FCSTD DOCUMENT  (FreeCAD 0.16R6712 (Git))
Label: EuW
License: All rights reserved
LicenseURL: http://en.wikipedia.org/wiki/All_rights_reserved
objects: Sketcher::SketchObject×21, PartDesign::Pad×11, PartDesign::Pocket×10, App::DocumentObjectGroup×5, Mesh::Feature×4, Spreadsheet::Sheet×3, Image::ImagePlane×1, Part::Mirroring×1
note: 64 computed .brp shape members not serialized (recipe doc carries the construction recipe); baked Part::Feature solids carry a one-line shape summary decoded from their .brp

FEATURE [Sketcher::SketchObject] Sketch
  sketch-geometry (6):
    g0: LineSegment StartX=-20.6532 StartY=-31.9378 StartZ=0 EndX=22.2568 EndY=-31.9378 EndZ=0
    g1: LineSegment StartX=22.2568 StartY=-31.9378 StartZ=0 EndX=22.2568 EndY=-20.3155 EndZ=0
    g2: LineSegment StartX=22.2568 StartY=-20.3155 StartZ=0 EndX=19.6468 EndY=-11.9755 EndZ=0
    g3: LineSegment StartX=19.6468 StartY=-11.9755 StartZ=0 EndX=19.6468 EndY=32.5722 EndZ=0
    g4: LineSegment StartX=19.6468 StartY=32.5722 StartZ=0 EndX=-20.6532 EndY=32.5722 EndZ=0
    g5: LineSegment StartX=-20.6532 StartY=32.5722 StartZ=0 EndX=-20.6532 EndY=-31.9378 EndZ=0
  constraints (14):
    c: Horizontal(g0)
    c: Coincident(g0,g1)
    c: Vertical(g1)
    c: Coincident(g1,g2)
    c: Coincident(g2,g3)
    c: Vertical(g3)
    c: Coincident(g3,g4)
    c: Horizontal(g4)
    c: Coincident(g4,g5)
    c: Coincident(g5,g0)
    c: Vertical(g5)
    c: DistanceX(g0,g0) = 42.91
    c: DistanceY(g0,g4) = 64.51
    c: DistanceX(g2,g1) = 2.61
FEATURE [Image::ImagePlane] ImagePlane
  XSize = 52.4742
  YSize = 69.419
FEATURE [PartDesign::Pad] Pad
  Length = 25
  Length2 = 100
  Sketch = -> Sketch
  Type = 0
FEATURE [Sketcher::SketchObject] Sketch001
  ExternalGeometry = -> [Pad]
  Placement = pos=(0,0,25) rot=(0,0,1;0rad)
  Support = -> Pad [Face8]
  sketch-geometry (2):
    g0: Circle CenterX=-12.8432 CenterY=15.3222 CenterZ=0 NormalX=0 NormalY=0 NormalZ=1 Radius=5.15
    g1: Circle CenterX=9.30682 CenterY=15.3222 CenterZ=0 NormalX=0 NormalY=0 NormalZ=1 Radius=5.15
  constraints (6):
    c: Radius(g0) = 5.15
    c: DistanceX(g-3,g0) = 7.81
    c: Equal(g0,g1) = 5.15
    c: DistanceY(g0,g-3) = 17.25
    c: DistanceY(g1,g-3) = 17.25
    c: DistanceX(g0,g1) = 22.15
FEATURE [PartDesign::Pocket] Pocket
  Length = 5
  Sketch = -> Sketch001
  Type = 1
FEATURE [Sketcher::SketchObject] Sketch002
  expr: Constraints[13] = Spreadsheet.E2
  expr: Constraints[12] = Spreadsheet.C2
  expr: Constraints[11] = Spreadsheet.B2
  sketch-geometry (6):
    g0: LineSegment StartX=-20.6044 StartY=-32.0766 StartZ=0 EndX=22.3056 EndY=-32.0766 EndZ=0
    g1: LineSegment StartX=22.3056 StartY=-32.0766 StartZ=0 EndX=22.3056 EndY=-20.3155 EndZ=0
    g2: LineSegment StartX=22.3056 StartY=-20.3155 StartZ=0 EndX=19.6956 EndY=-11.9755 EndZ=0
    g3: LineSegment StartX=19.6956 StartY=-11.9755 StartZ=0 EndX=19.6956 EndY=32.4334 EndZ=0
    g4: LineSegment StartX=19.6956 StartY=32.4334 StartZ=0 EndX=-20.6044 EndY=32.4334 EndZ=0
    g5: LineSegment StartX=-20.6044 StartY=32.4334 StartZ=0 EndX=-20.6044 EndY=-32.0766 EndZ=0
  constraints (14):
    c: Horizontal(g0)
    c: Coincident(g0,g1)
    c: Vertical(g1)
    c: Coincident(g1,g2)
    c: Coincident(g2,g3)
    c: Vertical(g3)
    c: Coincident(g3,g4)
    c: Horizontal(g4)
    c: Coincident(g4,g5)
    c: Coincident(g5,g0)
    c: Vertical(g5)
    c: DistanceX(g0,g0) = 42.91
    c: DistanceY(g0,g4) = 64.51
    c: DistanceX(g2,g1) = 2.61
FEATURE [Spreadsheet::Sheet] Spreadsheet
  cells = B1=Width; C1=Height; D1=Length; E1=Right Wing; F1=Position from top; G1=Position From Left; H1=Horizontal Dist; A2=Body; B2=42.91; C2=64.51000000000001; E2=2.61; A3=Bearing; B3==5 + B4; F3=17.25; G3==7.81 + 2.61; H3=22.15; A4=Clearence; B4=0.2
FEATURE [PartDesign::Pad] Pad001
  Length = 25
  Length2 = 100
  Sketch = -> Sketch002
  Type = 0
FEATURE [Sketcher::SketchObject] Sketch003
  ExternalGeometry = -> [Pad001]
  Placement = pos=(0,0,25) rot=(0,0,1;0rad)
  Support = -> Pad001 [Face8]
  expr: Constraints[5] = Spreadsheet.H3
  expr: Constraints[4] = Spreadsheet.F3
  expr: Constraints[2] = Spreadsheet.G3
  expr: Constraints[1] = Spreadsheet.F3
  expr: Constraints[0] = Spreadsheet.B3
  sketch-geometry (2):
    g0: Circle CenterX=-10.1844 CenterY=15.1834 CenterZ=0 NormalX=0 NormalY=0 NormalZ=1 Radius=5.2
    g1: Circle CenterX=11.9656 CenterY=15.1834 CenterZ=0 NormalX=0 NormalY=0 NormalZ=1 Radius=5.2
  constraints (6):
    c: Radius(g0) = 5.2
    c: DistanceY(g0,g-3) = 17.25
    c: DistanceX(g-3,g0) = 10.42
    c: Equal(g0,g1) = 5
    c: DistanceY(g1,g-3) = 17.25
    c: DistanceX(g0,g1) = 22.15
FEATURE [PartDesign::Pocket] Pocket001
  Length = 5
  Sketch = -> Sketch003
  Type = 1
FEATURE [App::DocumentObjectGroup] Gruppe  label="Body"
  Group = -> [ImagePlane,Pad,Pocket,Spreadsheet,Pad001,Pocket001]
FEATURE [Sketcher::SketchObject] Sketch004
  sketch-geometry (4):
    g0: LineSegment StartX=-7.22488 StartY=-3.31219 StartZ=0 EndX=4.67512 EndY=-3.31219 EndZ=0
    g1: LineSegment StartX=4.67512 StartY=-3.31219 StartZ=0 EndX=4.67512 EndY=-13.3122 EndZ=0
    g2: LineSegment StartX=4.67512 StartY=-13.3122 StartZ=0 EndX=-7.22488 EndY=-13.3122 EndZ=0
    g3: LineSegment StartX=-7.22488 StartY=-13.3122 StartZ=0 EndX=-7.22488 EndY=-3.31219 EndZ=0
  constraints (10):
    c: Coincident(g0,g1)
    c: Coincident(g1,g2)
    c: Coincident(g2,g3)
    c: Coincident(g3,g0)
    c: Horizontal(g0)
    c: Horizontal(g2)
    c: Vertical(g1)
    c: Vertical(g3)
    c: DistanceX(g0,g0) = 11.9
    c: DistanceY(g1,g1) = 10
FEATURE [PartDesign::Pad] Pad002
  Length = 7
  Length2 = 100
  Sketch = -> Sketch004
  Type = 0
FEATURE [Sketcher::SketchObject] Sketch005
  ExternalGeometry = -> [Pad002]
  Placement = pos=(0,0,7) rot=(0,0,1;0rad)
  Support = -> Pad002 [Face6]
  sketch-geometry (1):
    g0: Circle CenterX=-2.72488 CenterY=-8.31219 CenterZ=0 NormalX=0 NormalY=0 NormalZ=1 Radius=1.49
  constraints (3):
    c: DistanceX(g-3,g0) = 4.5
    c: DistanceY(g0,g-3) = 5
    c: Radius(g0) = 1.49
FEATURE [PartDesign::Pocket] Pocket002
  Length = 5
  Sketch = -> Sketch005
  Type = 1
FEATURE [Sketcher::SketchObject] Sketch006
  ExternalGeometry = -> [Pocket002]
  Placement = pos=(0,-13.3122,0) rot=(1,0,0;1.5708rad)
  Support = -> Pocket002 [Face6]
  sketch-geometry (4):
    g0: LineSegment StartX=-7.22488 StartY=4 StartZ=0 EndX=1.67512 EndY=4 EndZ=0
    g1: LineSegment StartX=1.67512 StartY=4 StartZ=0 EndX=1.67512 EndY=2.95 EndZ=0
    g2: LineSegment StartX=1.67512 StartY=2.95 StartZ=0 EndX=-7.22488 EndY=2.95 EndZ=0
    g3: LineSegment StartX=-7.22488 StartY=2.95 StartZ=0 EndX=-7.22488 EndY=4 EndZ=0
  constraints (12):
    c: Coincident(g0,g1)
    c: Coincident(g1,g2)
    c: Coincident(g2,g3)
    c: Coincident(g3,g0)
    c: Horizontal(g0)
    c: Horizontal(g2)
    c: Vertical(g1)
    c: Vertical(g3)
    c: DistanceX(g-3,g0) = 0
    c: DistanceX(g0,g0) = 8.9
    c: DistanceY(g1,g1) = 1.05
    c: DistanceY(g0,g-3) = 3
FEATURE [PartDesign::Pocket] Pocket003
  Length = 5
  Sketch = -> Sketch006
  Type = 1
FEATURE [App::DocumentObjectGroup] Gruppe002  label="slidestop"
  Group = -> [Pad002,Pocket002,Pocket003]
FEATURE [Mesh::Feature] board01
  Placement = pos=(0,0,3.2) rot=(0,0,1;0rad)
FEATURE [Mesh::Feature] board02
  Placement = pos=(0,0,-20) rot=(0,0,1;0rad)
FEATURE [Sketcher::SketchObject] Sketch007
  Placement = pos=(0.865,0,0) rot=(0,0,1;0rad)
  expr: Constraints[9] = Spreadsheet001.b_laenge
  expr: Constraints[8] = Spreadsheet001.b_breite
  sketch-geometry (4):
    g0: LineSegment StartX=-127.432 StartY=10.0331 StartZ=0 EndX=-0.432219 EndY=10.0331 EndZ=0
    g1: LineSegment StartX=-0.432219 StartY=-17.9669 StartZ=0 EndX=-127.432 EndY=-17.9669 EndZ=0
    g2: LineSegment StartX=-127.432 StartY=-17.9669 StartZ=0 EndX=-127.432 EndY=10.0331 EndZ=0
    g3: LineSegment StartX=-0.432219 StartY=10.0331 StartZ=0 EndX=-0.432219 EndY=-17.9669 EndZ=0
  constraints (10):
    c: Coincident(g1,g2)
    c: Coincident(g2,g0)
    c: Horizontal(g0)
    c: Horizontal(g1)
    c: Vertical(g2)
    c: Coincident(g3,g0)
    c: Coincident(g3,g1)
    c: Vertical(g3)
    c: DistanceY(g2,g2) = 28
    c: DistanceX(g0,g0) = 127
FEATURE [Spreadsheet::Sheet] Spreadsheet001
  cells = B1=Laenge; C1=Breite; D1=Höhe; A2=Board; B2(b_laenge)=127; C2(b_breite)=28; D2(b_hoehe)=6.8
FEATURE [PartDesign::Pad] Pad003
  Length = 6.8
  Length2 = 100
  Placement = pos=(0.865,0,0) rot=(0,0,1;0rad)
  Sketch = -> Sketch007
  Type = 0
  expr: Length = Spreadsheet001.b_hoehe
FEATURE [Sketcher::SketchObject] Sketch008
  ExternalGeometry = -> [Pad003]
  Placement = pos=(0.865,-17.9669,0) rot=(1,0,0;1.5708rad)
  Support = -> Pad003 [Face3]
  sketch-geometry (4):
    g0: LineSegment StartX=-127.432 StartY=6.8 StartZ=0 EndX=-125.932 EndY=6.8 EndZ=0
    g1: LineSegment StartX=-125.932 StartY=6.8 StartZ=0 EndX=-125.932 EndY=0 EndZ=0
    g2: LineSegment StartX=-125.932 StartY=0 StartZ=0 EndX=-127.432 EndY=0 EndZ=0
    g3: LineSegment StartX=-127.432 StartY=0 StartZ=0 EndX=-127.432 EndY=6.8 EndZ=0
  constraints (11):
    c: Coincident(g0,g1)
    c: Coincident(g1,g2)
    c: Coincident(g2,g3)
    c: Coincident(g3,g0)
    c: Horizontal(g0)
    c: Horizontal(g2)
    c: Vertical(g1)
    c: Vertical(g3)
    c: Coincident(g0,g-3)
    c: PointOnObject(g1,g-1)
    c: DistanceX(g0,g0) = 1.5
FEATURE [PartDesign::Pad] Pad004
  Length = 1.5
  Length2 = 100
  Placement = pos=(0.865,0,0) rot=(0,0,1;0rad)
  Sketch = -> Sketch008
  Type = 0
FEATURE [Sketcher::SketchObject] Sketch010
  ExternalGeometry = -> [Pad004]
  Placement = pos=(0.865,10.0331,0) rot=(0,0.707107,0.707107;3.14159rad)
  Support = -> Pad004 [Face1]
  sketch-geometry (4):
    g0: LineSegment StartX=127.432 StartY=6.8 StartZ=0 EndX=125.932 EndY=6.8 EndZ=0
    g1: LineSegment StartX=125.932 StartY=6.8 StartZ=0 EndX=125.932 EndY=0 EndZ=0
    g2: LineSegment StartX=125.932 StartY=0 StartZ=0 EndX=127.432 EndY=0 EndZ=0
    g3: LineSegment StartX=127.432 StartY=0 StartZ=0 EndX=127.432 EndY=6.8 EndZ=0
  constraints (11):
    c: Coincident(g0,g1)
    c: Coincident(g1,g2)
    c: Coincident(g2,g3)
    c: Coincident(g3,g0)
    c: Horizontal(g0)
    c: Horizontal(g2)
    c: Vertical(g1)
    c: Vertical(g3)
    c: Coincident(g0,g-3)
    c: PointOnObject(g1,g-1)
    c: DistanceX(g0,g0) = 1.5
FEATURE [PartDesign::Pad] Pad005
  Length = 1.5
  Length2 = 100
  Placement = pos=(0.865,0,0) rot=(0,0,1;0rad)
  Sketch = -> Sketch010
  Type = 0
FEATURE [Sketcher::SketchObject] Sketch012
  ExternalGeometry = -> [Pad005]
  Placement = pos=(0.865,0,6.8) rot=(0,0,1;0rad)
  Support = -> Pad005 [Face3]
  expr: Constraints[1] = Spreadsheet001.b_breite / 2 * -1
  sketch-geometry (1):
    g0: Circle CenterX=-56.4322 CenterY=-3.96691 CenterZ=0 NormalX=0 NormalY=0 NormalZ=1 Radius=3.03
  constraints (3):
    c: Radius(g0) = 3.03
    c: DistanceY(g-3,g0) = -14
    c: DistanceX(g-3,g0) = 69.5
FEATURE [PartDesign::Pocket] Pocket004
  Length = 5
  Placement = pos=(0.865,0,0) rot=(0,0,1;0rad)
  Sketch = -> Sketch012
  Type = 1
FEATURE [Sketcher::SketchObject] Sketch013
  ExternalGeometry = -> [Pocket004]
  Placement = pos=(0.865,-17.9669,0) rot=(1,0,0;1.5708rad)
  Support = -> Pocket004 [Face11]
  expr: Constraints[1] = Spreadsheet001.b_hoehe / 2
  sketch-geometry (3):
    g0: Circle CenterX=-56.4322 CenterY=3.4 CenterZ=0 NormalX=0 NormalY=0 NormalZ=1 Radius=1.05
    g1: Circle CenterX=-117.432 CenterY=3.4 CenterZ=0 NormalX=0 NormalY=0 NormalZ=1 Radius=1.5
    g2: Circle CenterX=-34.476 CenterY=3.4 CenterZ=0 NormalX=0 NormalY=0 NormalZ=1 Radius=1.5
  constraints (8):
    c: Radius(g0) = 1.05
    c: DistanceY(g0,g-3) = 3.4
    c: DistanceX(g-3,g0) = 69.5
    c: Radius(g1) = 1.5
    c: DistanceY(g0,g1) = 0
    c: DistanceX(g-3,g1) = 8.5
    c: Equal(g2,g1)
    c: DistanceY(g0,g2) = 0
FEATURE [PartDesign::Pocket] Pocket005
  Length = 5
  Placement = pos=(0.865,0,0) rot=(0,0,1;0rad)
  Sketch = -> Sketch013
  Type = 1
FEATURE [Sketcher::SketchObject] Sketch014
  ExternalGeometry = -> [Pocket005]
  Placement = pos=(0.865,0,0) rot=(1,0,0;3.14159rad)
  Support = -> Pocket005 [Face13]
  sketch-geometry (4):
    g0: LineSegment StartX=-101.432 StartY=14.3669 StartZ=0 EndX=-0.432219 EndY=14.3669 EndZ=0
    g1: LineSegment StartX=-0.432219 StartY=14.3669 StartZ=0 EndX=-0.432219 EndY=8.6669 EndZ=0
    g2: LineSegment StartX=-0.432219 StartY=8.6669 StartZ=0 EndX=-101.432 EndY=8.6669 EndZ=0
    g3: LineSegment StartX=-101.432 StartY=8.6669 StartZ=0 EndX=-101.432 EndY=14.3669 EndZ=0
  constraints (12):
    c: Coincident(g0,g1)
    c: Coincident(g1,g2)
    c: Coincident(g2,g3)
    c: Coincident(g3,g0)
    c: Horizontal(g0)
    c: Horizontal(g2)
    c: Vertical(g1)
    c: Vertical(g3)
    c: PointOnObject(g1,g-3)
    c: DistanceX(g0,g0) = 101
    c: DistanceY(g0,g-3) = 3.6
    c: DistanceY(g1,g0) = 5.7
FEATURE [PartDesign::Pocket] Pocket006
  Length = 1.69
  Placement = pos=(0.865,0,0) rot=(0,0,1;0rad)
  Sketch = -> Sketch014
  Type = 0
FEATURE [Mesh::Feature] board003
  Placement = pos=(0,0,3.2) rot=(0,0,1;0rad)
FEATURE [Mesh::Feature] board004
  Placement = pos=(0,0,-20) rot=(0,0,1;0rad)
FEATURE [Sketcher::SketchObject] Sketch015
  expr: Constraints[9] = Spreadsheet001.b_laenge
  expr: Constraints[8] = Spreadsheet001.b_breite
  sketch-geometry (4):
    g0: LineSegment StartX=-127.432 StartY=10.0331 StartZ=0 EndX=-0.432219 EndY=10.0331 EndZ=0
    g1: LineSegment StartX=-0.432219 StartY=-17.9669 StartZ=0 EndX=-127.432 EndY=-17.9669 EndZ=0
    g2: LineSegment StartX=-127.432 StartY=-17.9669 StartZ=0 EndX=-127.432 EndY=10.0331 EndZ=0
    g3: LineSegment StartX=-0.432219 StartY=10.0331 StartZ=0 EndX=-0.432219 EndY=-17.9669 EndZ=0
  constraints (10):
    c: Coincident(g1,g2)
    c: Coincident(g2,g0)
    c: Horizontal(g0)
    c: Horizontal(g1)
    c: Vertical(g2)
    c: Coincident(g3,g0)
    c: Coincident(g3,g1)
    c: Vertical(g3)
    c: DistanceY(g2,g2) = 28
    c: DistanceX(g0,g0) = 127
FEATURE [Spreadsheet::Sheet] Spreadsheet002
  cells = B1=Laenge; C1=Breite; D1=Höhe; A2=Board; B2(b_laenge)=127; C2(b_breite)=28; D2(b_hoehe)=6.8
FEATURE [PartDesign::Pad] Pad006
  Length = 6.8
  Length2 = 100
  Sketch = -> Sketch015
  Type = 0
  expr: Length = Spreadsheet001.b_hoehe
FEATURE [Sketcher::SketchObject] Sketch016
  ExternalGeometry = -> [Pad006]
  Placement = pos=(0,-17.9669,0) rot=(1,0,0;1.5708rad)
  Support = -> Pad006 [Face3]
  sketch-geometry (4):
    g0: LineSegment StartX=-127.432 StartY=6.8 StartZ=0 EndX=-125.932 EndY=6.8 EndZ=0
    g1: LineSegment StartX=-125.932 StartY=6.8 StartZ=0 EndX=-125.932 EndY=0 EndZ=0
    g2: LineSegment StartX=-125.932 StartY=0 StartZ=0 EndX=-127.432 EndY=0 EndZ=0
    g3: LineSegment StartX=-127.432 StartY=0 StartZ=0 EndX=-127.432 EndY=6.8 EndZ=0
  constraints (11):
    c: Coincident(g0,g1)
    c: Coincident(g1,g2)
    c: Coincident(g2,g3)
    c: Coincident(g3,g0)
    c: Horizontal(g0)
    c: Horizontal(g2)
    c: Vertical(g1)
    c: Vertical(g3)
    c: Coincident(g0,g-3)
    c: PointOnObject(g1,g-1)
    c: DistanceX(g0,g0) = 1.5
FEATURE [PartDesign::Pad] Pad007
  Length = 1.5
  Length2 = 100
  Sketch = -> Sketch016
  Type = 0
FEATURE [Sketcher::SketchObject] Sketch017
  ExternalGeometry = -> [Pad007]
  Placement = pos=(0,10.0331,0) rot=(0,0.707107,0.707107;3.14159rad)
  Support = -> Pad007 [Face1]
  sketch-geometry (4):
    g0: LineSegment StartX=127.432 StartY=6.8 StartZ=0 EndX=125.932 EndY=6.8 EndZ=0
    g1: LineSegment StartX=125.932 StartY=6.8 StartZ=0 EndX=125.932 EndY=0 EndZ=0
    g2: LineSegment StartX=125.932 StartY=0 StartZ=0 EndX=127.432 EndY=0 EndZ=0
    g3: LineSegment StartX=127.432 StartY=0 StartZ=0 EndX=127.432 EndY=6.8 EndZ=0
  constraints (11):
    c: Coincident(g0,g1)
    c: Coincident(g1,g2)
    c: Coincident(g2,g3)
    c: Coincident(g3,g0)
    c: Horizontal(g0)
    c: Horizontal(g2)
    c: Vertical(g1)
    c: Vertical(g3)
    c: Coincident(g0,g-3)
    c: PointOnObject(g1,g-1)
    c: DistanceX(g0,g0) = 1.5
FEATURE [PartDesign::Pad] Pad008
  Length = 1.5
  Length2 = 100
  Sketch = -> Sketch017
  Type = 0
FEATURE [Sketcher::SketchObject] Sketch018
  ExternalGeometry = -> [Pad008]
  Placement = pos=(0,0,6.8) rot=(0,0,1;0rad)
  Support = -> Pad008 [Face3]
  expr: Constraints[1] = Spreadsheet001.b_breite / 2 * -1
  sketch-geometry (1):
    g0: Circle CenterX=-56.4322 CenterY=-3.96691 CenterZ=0 NormalX=0 NormalY=0 NormalZ=1 Radius=3.03
  constraints (3):
    c: Radius(g0) = 3.03
    c: DistanceY(g-3,g0) = -14
    c: DistanceX(g-3,g0) = 69.5
FEATURE [PartDesign::Pocket] Pocket007
  Length = 5
  Sketch = -> Sketch018
  Type = 1
FEATURE [Sketcher::SketchObject] Sketch019
  ExternalGeometry = -> [Pocket007]
  Placement = pos=(0,-17.9669,0) rot=(1,0,0;1.5708rad)
  Support = -> Pocket007 [Face11]
  expr: Constraints[1] = Spreadsheet001.b_hoehe / 2
  sketch-geometry (3):
    g0: Circle CenterX=-56.4322 CenterY=3.4 CenterZ=0 NormalX=0 NormalY=0 NormalZ=1 Radius=1.05
    g1: Circle CenterX=-117.432 CenterY=3.4 CenterZ=0 NormalX=0 NormalY=0 NormalZ=1 Radius=1.5
    g2: Circle CenterX=-34.476 CenterY=3.4 CenterZ=0 NormalX=0 NormalY=0 NormalZ=1 Radius=1.5
  constraints (8):
    c: Radius(g0) = 1.05
    c: DistanceY(g0,g-3) = 3.4
    c: DistanceX(g-3,g0) = 69.5
    c: Radius(g1) = 1.5
    c: DistanceY(g0,g1) = 0
    c: DistanceX(g-3,g1) = 8.5
    c: Equal(g2,g1)
    c: DistanceY(g0,g2) = 0
FEATURE [PartDesign::Pocket] Pocket008
  Length = 5
  Sketch = -> Sketch019
  Type = 1
FEATURE [Sketcher::SketchObject] Sketch020
  ExternalGeometry = -> [Pocket008]
  Placement = pos=(0,0,0) rot=(1,0,0;3.14159rad)
  Support = -> Pocket008 [Face13]
  sketch-geometry (4):
    g0: LineSegment StartX=-101.432 StartY=14.3669 StartZ=0 EndX=-0.432219 EndY=14.3669 EndZ=0
    g1: LineSegment StartX=-0.432219 StartY=14.3669 StartZ=0 EndX=-0.432219 EndY=8.6669 EndZ=0
    g2: LineSegment StartX=-0.432219 StartY=8.6669 StartZ=0 EndX=-101.432 EndY=8.6669 EndZ=0
    g3: LineSegment StartX=-101.432 StartY=8.6669 StartZ=0 EndX=-101.432 EndY=14.3669 EndZ=0
  constraints (12):
    c: Coincident(g0,g1)
    c: Coincident(g1,g2)
    c: Coincident(g2,g3)
    c: Coincident(g3,g0)
    c: Horizontal(g0)
    c: Horizontal(g2)
    c: Vertical(g1)
    c: Vertical(g3)
    c: PointOnObject(g1,g-3)
    c: DistanceX(g0,g0) = 101
    c: DistanceY(g0,g-3) = 3.6
    c: DistanceY(g1,g0) = 5.7
FEATURE [PartDesign::Pocket] Pocket009
  Length = 1.69
  Sketch = -> Sketch020
  Type = 0
FEATURE [Part::Mirroring] Part__Mirroring  label="Pocket009 (Mirror #1)"
  Base = (0,0,0)
  Normal = (1,0,0)
  Source = -> Pocket009
FEATURE [Sketcher::SketchObject] Sketch021
  ExternalGeometry = -> [Pocket006]
  Placement = pos=(0.432781,0,0) rot=(0.57735,0.57735,0.57735;2.0944rad)
  Support = -> Pocket006 [Face10]
  expr: Constraints[11] = Spreadsheet001.b_breite / 2 - 3.5
  expr: Constraints[10] = Spreadsheet001.b_hoehe / 2
  sketch-geometry (4):
    g0: LineSegment StartX=-7.4669 StartY=3.4 StartZ=0 EndX=-0.466905 EndY=3.4 EndZ=0
    g1: LineSegment StartX=-0.466905 StartY=3.4 StartZ=0 EndX=-0.466905 EndY=0 EndZ=0
    g2: LineSegment StartX=-0.466905 StartY=0 StartZ=0 EndX=-7.4669 EndY=0 EndZ=0
    g3: LineSegment StartX=-7.4669 StartY=0 StartZ=0 EndX=-7.4669 EndY=3.4 EndZ=0
  constraints (12):
    c: Coincident(g0,g1)
    c: Coincident(g1,g2)
    c: Coincident(g2,g3)
    c: Coincident(g3,g0)
    c: Horizontal(g0)
    c: Horizontal(g2)
    c: Vertical(g1)
    c: Vertical(g3)
    c: PointOnObject(g1,g-3)
    c: DistanceX(g0,g0) = 7
    c: DistanceY(g1,g0) = 3.4
    c: DistanceX(g1,g-3) = 10.5
FEATURE [PartDesign::Pad] Pad009
  Length = 7
  Length2 = 100
  Placement = pos=(0.865,0,0) rot=(0,0,1;0rad)
  Sketch = -> Sketch021
  Type = 0
FEATURE [App::DocumentObjectGroup] Gruppe003  label="Board001"
  Group = -> [board01,board02,Pad003,Pad004,Pad005,Pocket004,Pocket005,Pocket006,Spreadsheet002,Pad009]
FEATURE [Sketcher::SketchObject] Sketch022
  ExternalGeometry = -> [Part__Mirroring]
  Placement = pos=(0.432219,0,0) rot=(0.57735,-0.57735,-0.57735;2.0944rad)
  Support = -> Part__Mirroring [Face10]
  expr: Constraints[9] = Spreadsheet001.b_hoehe / 2
  sketch-geometry (8):
    g0: LineSegment StartX=-7.0331 StartY=6.8 StartZ=0 EndX=-2.03309 EndY=6.8 EndZ=0
    g1: LineSegment StartX=-2.03309 StartY=6.8 StartZ=0 EndX=-2.03309 EndY=3.4 EndZ=0
    g2: LineSegment StartX=-2.03309 StartY=3.4 StartZ=0 EndX=-7.0331 EndY=3.4 EndZ=0
    g3: LineSegment StartX=-7.0331 StartY=3.4 StartZ=0 EndX=-7.0331 EndY=6.8 EndZ=0
    g4: LineSegment StartX=9.96691 StartY=6.8 StartZ=0 EndX=14.9669 EndY=6.8 EndZ=0
    g5: LineSegment StartX=14.9669 StartY=6.8 StartZ=0 EndX=14.9669 EndY=3.4 EndZ=0
    g6: LineSegment StartX=14.9669 StartY=3.4 StartZ=0 EndX=9.96691 EndY=3.4 EndZ=0
    g7: LineSegment StartX=9.96691 StartY=3.4 StartZ=0 EndX=9.96691 EndY=6.8 EndZ=0
  constraints (24):
    c: Coincident(g0,g1)
    c: Coincident(g1,g2)
    c: Coincident(g2,g3)
    c: Coincident(g3,g0)
    c: Horizontal(g0)
    c: Horizontal(g2)
    c: Vertical(g1)
    c: Vertical(g3)
    c: PointOnObject(g0,g-3)
    c: DistanceY(g1,g1) = 3.4
    c: DistanceX(g-3,g0) = 3
    c: DistanceX(g2,g2) = 5
    c: Coincident(g4,g5)
    c: Coincident(g5,g6)
    c: Coincident(g6,g7)
    c: Coincident(g7,g4)
    c: Horizontal(g4)
    c: Horizontal(g6)
    c: Vertical(g5)
    c: Vertical(g7)
    c: PointOnObject(g4,g-3)
    c: Equal(g7,g1)
    c: Equal(g6,g2)
    c: DistanceX(g4,g-3) = 3
FEATURE [PartDesign::Pad] Pad010
  Length = 7
  Length2 = 100
  Sketch = -> Sketch022
  Type = 0
FEATURE [App::DocumentObjectGroup] Gruppe004  label="Board002"
  Group = -> [board003,board004,Pad006,Pad007,Pad008,Pocket007,Pocket008,Pocket009,Part__Mirroring,Pad010]
FEATURE [App::DocumentObjectGroup] Gruppe001  label="Board"
  Group = -> [Gruppe002,Gruppe003,Gruppe004]
